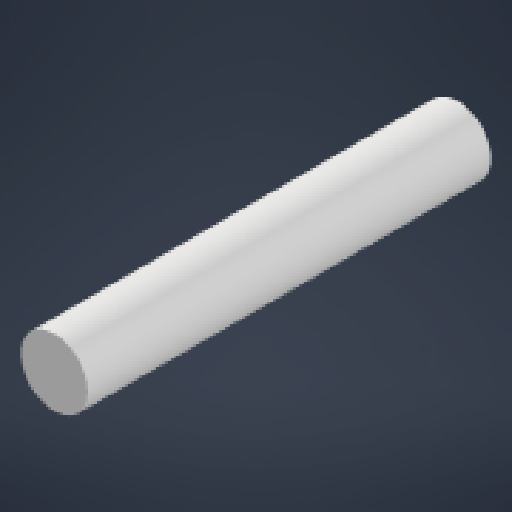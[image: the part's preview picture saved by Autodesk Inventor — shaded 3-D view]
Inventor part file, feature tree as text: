
AUTODESK INVENTOR PART (.ipt)
format: ipt  version: 2024 (Build 280153000, 153)  size: 130,048 bytes
history: native  units: mm
features: extrude x2, other x1, sketch x1
ambient origin geometry x8: Origin, YZ Plane, XZ Plane, XY Plane, X Axis, Y Axis, Z Axis, Center Point
bodies: Body1 (feature_tree)
feature tree (4):
  other  "솔리드1"
  sketch  "스케치1"
  extrude  "돌출1"  Depth=10.0mm
  extrude  "돌출2"  Depth=5.0mm
